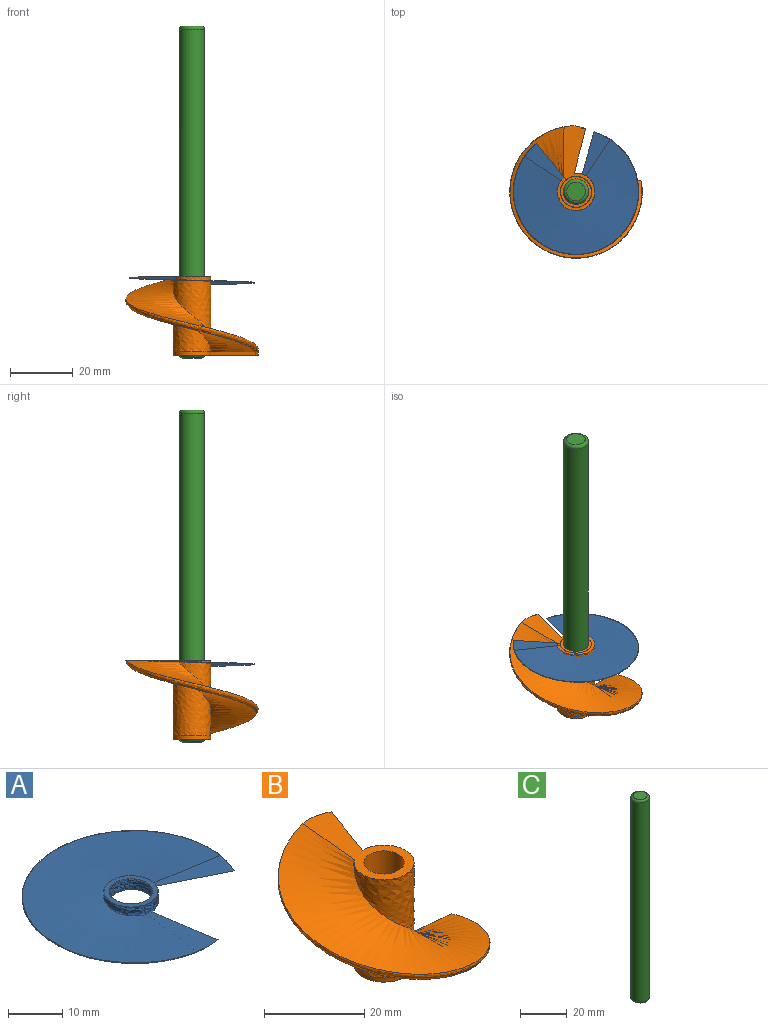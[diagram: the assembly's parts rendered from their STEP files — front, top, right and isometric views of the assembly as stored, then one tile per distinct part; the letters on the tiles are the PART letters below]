
ASSEMBLY  parts=3 mates=2
PART A: 7 faces, bbox 43.5x42.9x2.4 mm
  f0: bspline ~19.56x19.55mm, area 60.4mm2, adj f1,f2
  f1: plane 25.02x10mm, normal (0,0,-1), area 78.8mm2, adj f0,f3,f4,f5,f6
  f2: plane 24.7x13.78mm, normal (0,0,1), area 78.8mm2, adj f0,f3,f4,f5,f6
  f3: bspline ~22.47x22.39mm, area 72.8mm2, adj f1,f2,f4,f6
  f4: bspline ~39.99x39.8mm, area 943.4mm2, adj f1,f2,f3,f5
  f5: bspline ~43.54x42.89mm, area 14mm2, adj f1,f2,f4,f6
  f6: bspline ~41.62x41.54mm, area 943.4mm2, adj f1,f2,f3,f5
PART B: 11 faces, bbox 43.3x43.5x27.7 mm
  f0: plane 16.17x1.64mm, normal (0.1,0.99,0), area 16.3mm2, adj f1,f3,f4,f5
  f1: cylinder r=6mm len=12mm, axis (0,0,-1), area 33.9mm2, adj f0,f2,f4,f6
  f2: plane 13.8x4.92mm, normal (-0.34,-0.94,0), area 14.6mm2, adj f1,f3,f4,f7
  f3: cylinder r=10.08mm len=6.83mm, axis (0,0,-1), area 7.1mm2, adj f0,f2,f4,f8
  f4: plane 27.16x12mm, normal (0,0,-1), area 142.9mm2, adj f0,f1,f2,f3,f10
  f5: bspline ~43.03x43.03mm, area 1049.5mm2, adj f0,f6,f8,f9
  f6: bspline ~26.67x22.4mm, area 813.3mm2, adj f1,f5,f7,f9
  f7: bspline ~42.23x40.91mm, area 968.8mm2, adj f2,f6,f8,f9
  f8: bspline ~43.53x43.28mm, area 195.1mm2, adj f3,f5,f7,f9
  f9: plane 27.16x12mm, normal (0,0,1), area 142.9mm2, adj f5,f6,f7,f8,f10
  f10: cylinder r=4mm len=25mm, axis (0,0,-1), area 628.3mm2, adj f4,f9
PART C: 5 faces, bbox 8.7x8.7x106 mm
  f0: cylinder r=4mm len=104mm, axis (0,0,-1), area 2613.8mm2, adj f3,f4
  f1: plane 6x6mm, normal (0,0,1), area 28.3mm2, adj f4
  f2: plane 6x6mm, normal (0,0,-1), area 28.3mm2, adj f3
  f3: torus R=3mm, axis (0,0,1), area 35.9mm2, adj f0,f2
  f4: torus R=3mm, axis (0,0,1), area 35.9mm2, adj f0,f1
PLACE A rot(axis=(0,0,1),155.1deg) t=(0,0,23.51)mm
PLACE B rot(axis=(0,0,1),5.2deg) t=(0,0,0.94)mm
PLACE C at identity fixed
MATE cylindrical B.f10 <-> C.f0  axis (0,0,1) through (0,0,25.94)mm
MATE cylindrical A.f1 <-> C.f0  axis (0,0,-1) through (0,0,23.51)mm
